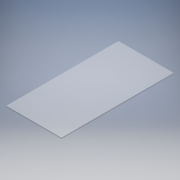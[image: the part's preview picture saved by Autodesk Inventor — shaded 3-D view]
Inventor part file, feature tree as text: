
AUTODESK INVENTOR PART (.ipt)
format: ipt  version: 2018 (Build 220112000, 112)  size: 109,568 bytes
history: native  units: mm
features: extrude x1, sketch x1
ambient origin geometry x8: Origin, YZ Plane, XZ Plane, XY Plane, X Axis, Y Axis, Z Axis, Center Point
bodies: Volumenkörper1 (feature_tree)
feature tree (2):
  extrude  "Extrusion1"  Depth=287.0mm
  sketch  "Skizze1"  dims[d0=583.0mm d1=287.0mm d2=6.0mm d3=0.0mm]
